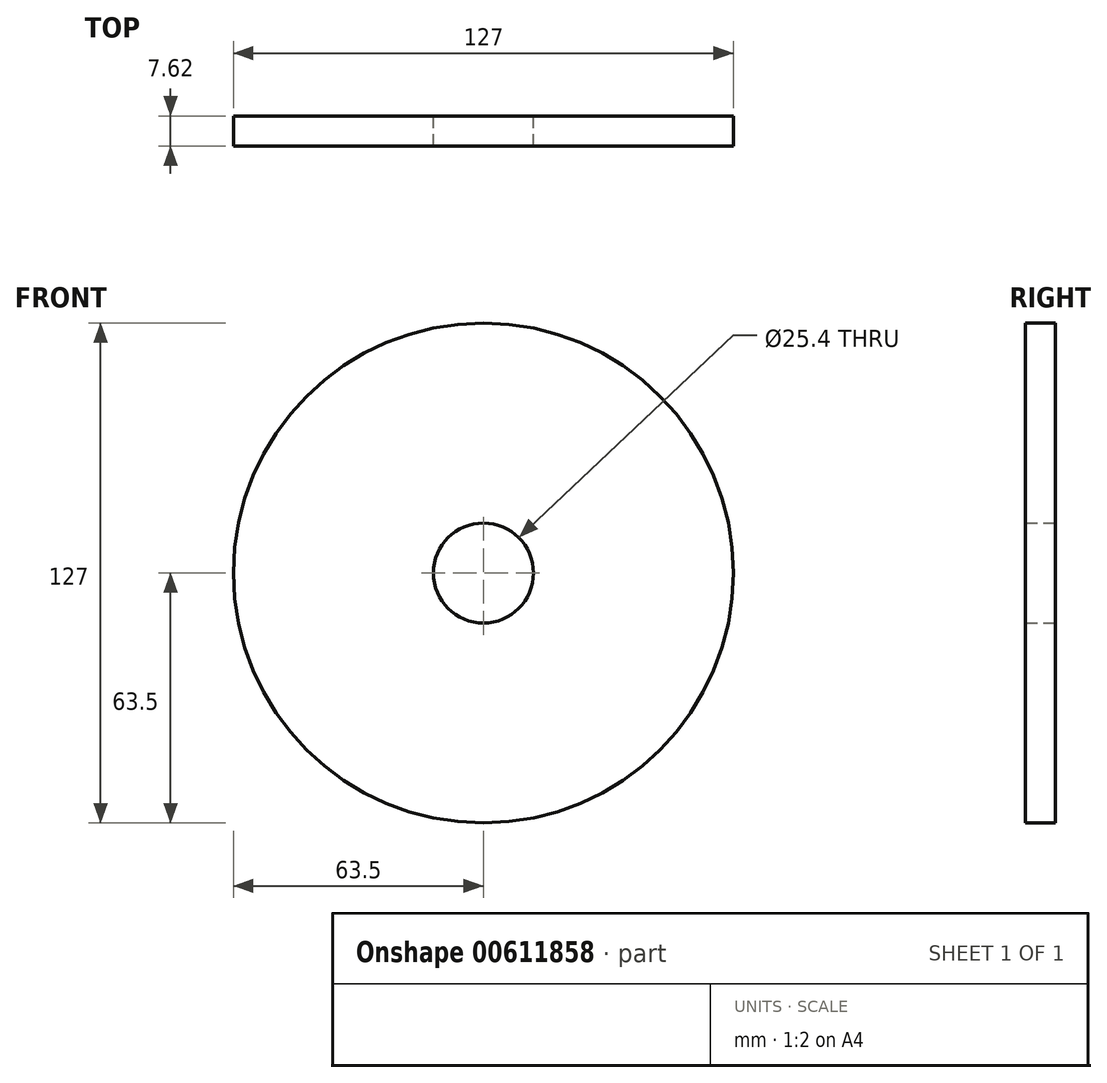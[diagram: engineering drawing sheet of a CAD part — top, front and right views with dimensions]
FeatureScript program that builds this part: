
annotation { "Feature Type Name" : "Feature", "Feature Type Description" : "" }
export const myFeature = defineFeature(function(context is Context, id is Id, definition is map)
    precondition{}
    {
        {
            var Q0;
            Q0=qCreatedBy(makeId("Front.planeOp"),FACE);
            var sketch = newSketch(context, id + "F0", { "sketchPlane" : qUnion([Q0])});
            skCircle(sketch, "E0", {"center": v(0, 0) * mm, "radius": 12.7 * mm});
            skCircle(sketch, "E1", {"center": v(0, 0) * mm, "radius": 63.5 * mm});
            skSolve(sketch);
        }
        {
            var Q0;
            Q0=makeQuery(id+"F0.imprint","IMPRINT",FACE,{"disambiguationData":[TD([[makeQuery(id+"F0.imprint","IMPRINT",EDGE,{"derivedFrom":sQuery(id+"F0.wireOp",EDGE,"E0")}),-1.0]])]});
            extrude(context, id + "F1", {"entities" : qUnion([Q0]), "endBound" : BoundingType.SYMMETRIC, "depth" : 7.62 * mm, "offsetDistance" : 25.4 * mm});
        }
        {
            var Q0;
            Q0=qCreatedBy(makeId("Front.planeOp"),FACE);
            var sketch = newSketch(context, id + "F2", { "sketchPlane" : qUnion([Q0])});
            skCircle(sketch, "E2", {"center": v(0, 0) * mm, "radius": 19.05 * mm});
            skCircle(sketch, "E3", {"center": v(-13.75, 7.94) * mm, "radius": 1.27 * mm});
            skCircle(sketch, "E4", {"center": v(0, 15.88) * mm, "radius": 1.27 * mm});
            skCircle(sketch, "E5", {"center": v(13.75, 7.94) * mm, "radius": 1.27 * mm});
            skCircle(sketch, "E6", {"center": v(13.75, -7.94) * mm, "radius": 1.27 * mm});
            skCircle(sketch, "E7", {"center": v(0, -15.88) * mm, "radius": 1.27 * mm});
            skCircle(sketch, "E8", {"center": v(-13.75, -7.94) * mm, "radius": 1.27 * mm});
            skCircle(sketch, "E9", {"center": v(0, 0) * mm, "radius": 12.7 * mm});
            skSolve(sketch);
        }
        {
            var Q0;
            Q0=sQuery(id+"F2.wireOp",EDGE,"E2");
            var Q1;
            Q1=sQuery(id+"F2.wireOp",EDGE,"E9");
            var Q2;
            Q2=sQuery(id+"F2.wireOp",EDGE,"E3");
            var Q3;
            Q3=sQuery(id+"F2.wireOp",EDGE,"E8");
            var Q4;
            Q4=sQuery(id+"F2.wireOp",EDGE,"E7");
            var Q5;
            Q5=sQuery(id+"F2.wireOp",EDGE,"E6");
            var Q6;
            Q6=sQuery(id+"F2.wireOp",EDGE,"E5");
            var Q7;
            Q7=sQuery(id+"F2.wireOp",EDGE,"E4");
            extrude(context, id + "F3", {"bodyType" : ToolBodyType.SURFACE, "operationType" : NewBodyOperationType.ADD, "surfaceEntities" : qUnion([Q0, Q1, Q2, Q3, Q4, Q5, Q6, Q7]), "endBound" : BoundingType.SYMMETRIC, "depth" : 12.7 * mm, "offsetDistance" : 25.4 * mm});
        }
    });
